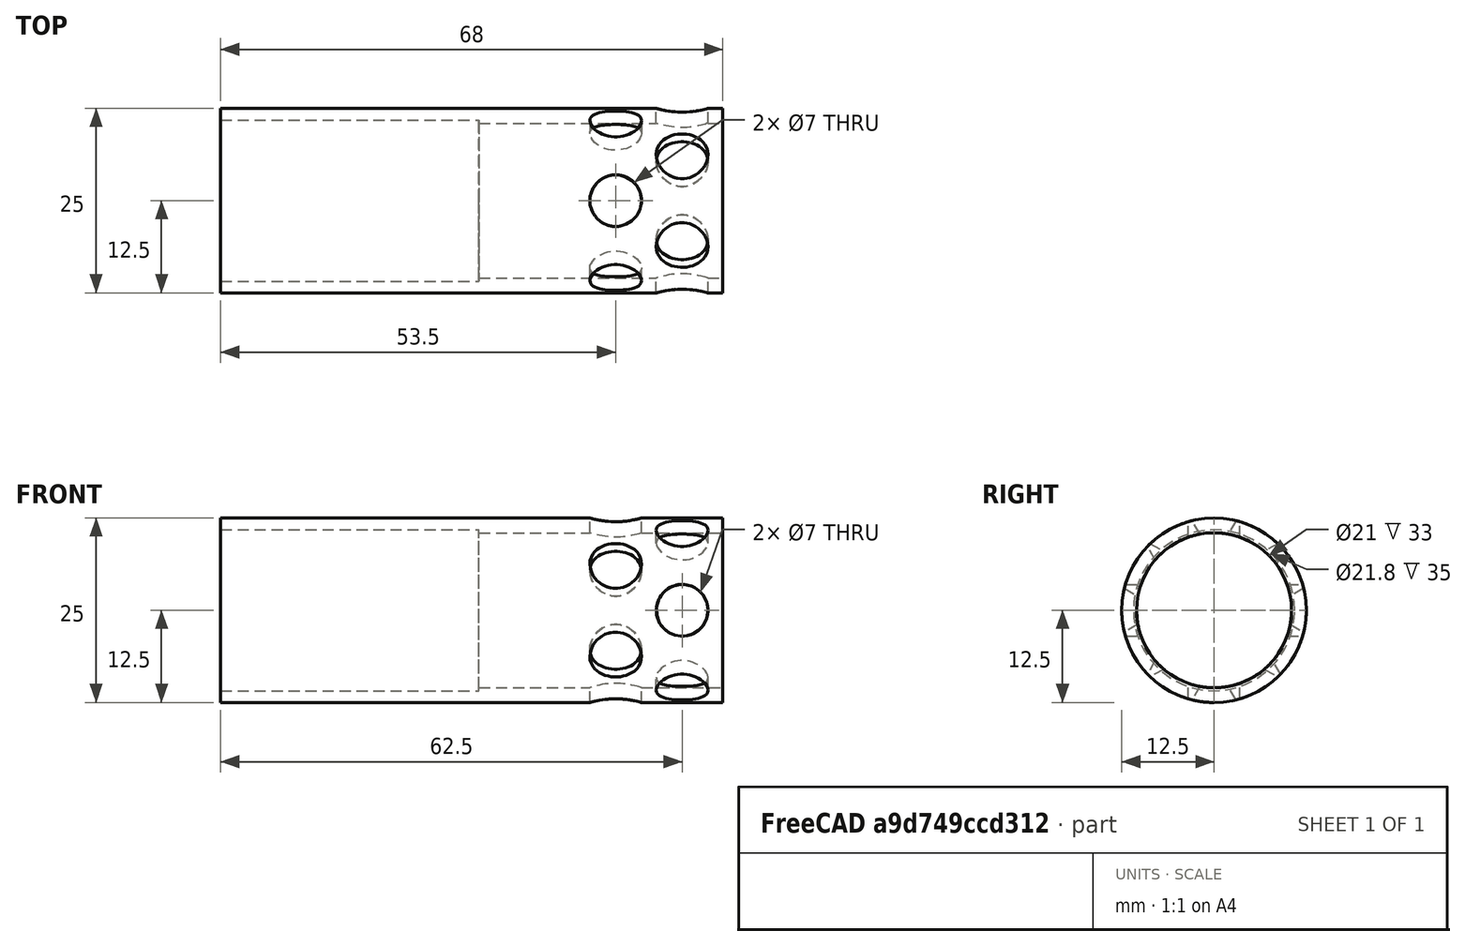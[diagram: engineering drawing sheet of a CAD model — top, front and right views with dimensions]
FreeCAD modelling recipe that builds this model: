
FCSTD DOCUMENT  (FreeCAD 0.17R13541 (Git))
Label: ERG-T-04-SC-01
License: All rights reserved
LicenseURL: http://en.wikipedia.org/wiki/All_rights_reserved
objects: Drawing::FeatureViewPython×12, Part::Cylinder×9, Part::MultiFuse×4, Part::Cut×2, Drawing::FeatureViewPart×2, Drawing::FeaturePage×1
note: 15 computed .brp shape members not serialized (recipe doc carries the construction recipe); baked Part::Feature solids carry a one-line shape summary decoded from their .brp

FEATURE [Part::Cylinder] Cylinder070  label="Cylinder075"
  Angle = 360
  AttacherType = Attacher::AttachEngine3D
  Height = 50
  Placement = pos=(214.2,-21.6506,12.5) rot=(-1,0,0;2.0944rad)
  Radius = 3.5
FEATURE [Part::Cylinder] Cylinder073  label="Cylinder082"
  Angle = 360
  AttacherType = Attacher::AttachEngine3D
  Height = 50
  Placement = pos=(214.2,-21.6506,12.5) rot=(-1,0,0;2.0944rad)
  Radius = 3.5
FEATURE [Part::Cylinder] Cylinder078  label="Cylinder087"
  Angle = 360
  AttacherType = Attacher::AttachEngine3D
  Height = 50
  Placement = pos=(214.2,21.6506,12.5) rot=(1,0,0;2.0944rad)
  Radius = 3.5
FEATURE [Part::Cylinder] Cylinder079  label="Cylinder088"
  Angle = 360
  AttacherType = Attacher::AttachEngine3D
  Height = 50
  Placement = pos=(214.2,21.6506,12.5) rot=(1,0,0;2.0944rad)
  Radius = 3.5
FEATURE [Part::Cylinder] Cylinder081  label="Cylinder090"
  Angle = 360
  AttacherType = Attacher::AttachEngine3D
  Height = 50
  Placement = pos=(214.2,0,-25) rot=(0,1,0;0rad)
  Radius = 3.5
FEATURE [Part::MultiFuse] Fusion016
  Placement = pos=(37.5,0,0) rot=(1,0,0;0rad)
  Shapes = -> [Cylinder081,Cylinder070,Cylinder078]
FEATURE [Part::Cylinder] Cylinder082  label="Cylinder078"
  Angle = 360
  AttacherType = Attacher::AttachEngine3D
  Height = 50
  Placement = pos=(214.2,0,-25) rot=(0,1,0;0rad)
  Radius = 3.5
FEATURE [Part::MultiFuse] Fusion018
  Placement = pos=(46.5,0,0) rot=(1,0,0;0.523599rad)
  Shapes = -> [Cylinder082,Cylinder073,Cylinder079]
FEATURE [Part::MultiFuse] Fusion  label="holesticks"
  Shapes = -> [Fusion016,Fusion018]
FEATURE [Part::Cylinder] Cylinder090  label="Cylinder098"
  Angle = 360
  AttacherType = Attacher::AttachEngine3D
  Height = 68
  Placement = pos=(198.2,0,0) rot=(0,1,0;1.5708rad)
  Radius = 12.5
FEATURE [Part::Cylinder] Cylinder071  label="Cylinder081"
  Angle = 360
  AttacherType = Attacher::AttachEngine3D
  Height = 33
  Placement = pos=(233.2,0,0) rot=(0,1,0;1.5708rad)
  Radius = 10.5
FEATURE [Part::Cylinder] Cylinder091  label="Cylinder099"
  Angle = 360
  AttacherType = Attacher::AttachEngine3D
  Height = 35
  Placement = pos=(198.2,0,0) rot=(0,1,0;1.5708rad)
  Radius = 10.9
FEATURE [Part::MultiFuse] Fusion019  label="cavity"
  Shapes = -> [Cylinder091,Cylinder071]
FEATURE [Part::Cut] Cut  label="body"
  Base = -> Cylinder090
  Tool = -> Fusion019
FEATURE [Part::Cut] Cut001  label="cap"
  Base = -> Cut
  Tool = -> Fusion
FEATURE [Drawing::FeatureViewPart] Ortho  label="Ortho_0_0"
  Direction = (1,0,0)
  HiddenWidth = 0.15
  LineWidth = 0.35
  Rotation = -90
  Scale = 2
  ShowHiddenLines = true
  ShowSmoothLines = false
  Source = -> Cut001
  Tolerance = 0.05
  ViewResult = <blob: 35669 chars omitted>
  Visible = true
  X = 65.3333
  Y = 81.5
FEATURE [Drawing::FeatureViewPart] Ortho001  label="Ortho_1_0"
  Direction = (0,1,0)
  HiddenWidth = 0.15
  LineWidth = 0.35
  Rotation = -90
  Scale = 2
  ShowHiddenLines = true
  ShowSmoothLines = false
  Source = -> Cut001
  Tolerance = 0.05
  ViewResult = <blob: 45142 chars omitted>
  Visible = true
  X = 653.067
  Y = 81.5
FEATURE [Drawing::FeatureViewPython] dim001  # drawing view (typed FeaturePython)
  Rotation = 0
  ViewResult = <g> \n  <line x1="120.667000" y1="56.500000" x2="120.667000" y2="35.635812" style="stroke:rgb(255,0,0);stroke-width:0.10" />\n<line x1="256.667000" y1="56.500000" x2="256.667000" y2="35.635812" style="stroke:rgb(255,0,0);stroke-width:0.10" />\n<line x1="120.667000" y1="36.635812" x2="256.667000" y2="36.635812" style="stroke:rgb(255,0,0);stroke-width:0.10" /> \n  <polygon points="256.667000,36.635812 254.667000,36.135812 254.167000,36.635812 254.667000,37.135812" style="fill:rgb(255,0,0);stroke:rgb(255,0,0);stroke-width:0" /><polygon points="120.667000,36.635812 122.667000,37.135812 123.167000,36.635812 122.667000,36.135812" style="fill:rgb(255,0,0);stroke:rgb(255,0,0);stroke-width:0" /> \n  <text x="188.667000" y="34.635812" font-family="inherit" font-size="3.6" fill="rgb(0,0,0)" text-anchor="middle" transform="rotate(0.000000 188.667000,34.635812)" >68</text> </g>
  Visible = true
  X = 0
  Y = 0
  arrowL1 = 2
  arrowL2 = 0.5
  arrowW = 1
  arrow_scheme = 0
  autoPlaceOffset = 2
  autoPlaceText = true
  click1_x = 255.659
  click1_y = 36.6358
  click2_x = 255.659
  click2_y = 36.6358
  comma_decimal_place = false
  dimension_line_overshoot = 1
  gap_datum_points = 0
  halfDimension_linear = false
  lineColor = rgb(255,0,0)
  strokeWidth = 0.1
  textFormat_linear = %(value)3.3f
  textRenderer_color = rgb(0,0,0)
  textRenderer_family = inherit
  textRenderer_size = 3.6
  unit_custom_scale = 1
  unit_scheme = 0
FEATURE [Drawing::FeatureViewPython] dim005  # drawing view (typed FeaturePython)
  Rotation = 0
  ViewResult = <g> \n  <line x1="256.667000" y1="106.500000" x2="279.698064" y2="106.500000" style="stroke:rgb(255,0,0);stroke-width:0.10" />\n<line x1="256.667000" y1="56.500000" x2="279.698064" y2="56.500000" style="stroke:rgb(255,0,0);stroke-width:0.10" />\n<line x1="278.698064" y1="106.500000" x2="278.698064" y2="56.500000" style="stroke:rgb(255,0,0);stroke-width:0.10" /> \n  <polygon points="278.698064,56.500000 278.198064,58.500000 278.698064,59.000000 279.198064,58.500000" style="fill:rgb(255,0,0);stroke:rgb(255,0,0);stroke-width:0" /><polygon points="278.698064,106.500000 279.198064,104.500000 278.698064,104.000000 278.198064,104.500000" style="fill:rgb(255,0,0);stroke:rgb(255,0,0);stroke-width:0" /> \n  <text x="276.698064" y="81.500000" font-family="inherit" font-size="3.6" fill="rgb(0,0,0)" text-anchor="middle" transform="rotate(-90.000000 276.698064,81.500000)" >25</text> </g>
  Visible = true
  X = 0
  Y = 0
  arrowL1 = 2
  arrowL2 = 0.5
  arrowW = 1
  arrow_scheme = 0
  autoPlaceOffset = 2
  autoPlaceText = true
  click1_x = 278.698
  click1_y = 57.3499
  click2_x = 278.698
  click2_y = 57.3499
  comma_decimal_place = false
  dimension_line_overshoot = 1
  gap_datum_points = 0
  halfDimension_linear = false
  lineColor = rgb(255,0,0)
  strokeWidth = 0.1
  textFormat_linear = %(value)3.3f
  textRenderer_color = rgb(0,0,0)
  textRenderer_family = inherit
  textRenderer_size = 3.6
  unit_custom_scale = 1
  unit_scheme = 0
FEATURE [Drawing::FeatureViewPython] dim006  # drawing view (typed FeaturePython)
  Rotation = 0
  ViewResult = <g> \n  <line x1="256.667000" y1="103.300000" x2="248.784893" y2="103.300000" style="stroke:rgb(255,0,0);stroke-width:0.10" />\n<line x1="256.667000" y1="59.700000" x2="248.784893" y2="59.700000" style="stroke:rgb(255,0,0);stroke-width:0.10" />\n<line x1="249.784893" y1="103.300000" x2="249.784893" y2="59.700000" style="stroke:rgb(255,0,0);stroke-width:0.10" /> \n  <polygon points="249.784893,59.700000 249.284893,61.700000 249.784893,62.200000 250.284893,61.700000" style="fill:rgb(255,0,0);stroke:rgb(255,0,0);stroke-width:0" /><polygon points="249.784893,103.300000 250.284893,101.300000 249.784893,100.800000 249.284893,101.300000" style="fill:rgb(255,0,0);stroke:rgb(255,0,0);stroke-width:0" /> \n  <text x="247.784893" y="81.500000" font-family="inherit" font-size="3.6" fill="rgb(0,0,0)" text-anchor="middle" transform="rotate(-90.000000 247.784893,81.500000)" >21.8</text> </g>
  Visible = true
  X = 0
  Y = 0
  arrowL1 = 2
  arrowL2 = 0.5
  arrowW = 1
  arrow_scheme = 0
  autoPlaceOffset = 2
  autoPlaceText = true
  click1_x = 249.785
  click1_y = 59.7094
  click2_x = 249.785
  click2_y = 59.7094
  comma_decimal_place = false
  dimension_line_overshoot = 1
  gap_datum_points = 0
  halfDimension_linear = false
  lineColor = rgb(255,0,0)
  strokeWidth = 0.1
  textFormat_linear = %(value)3.3f
  textRenderer_color = rgb(0,0,0)
  textRenderer_family = inherit
  textRenderer_size = 3.6
  unit_custom_scale = 1
  unit_scheme = 0
FEATURE [Drawing::FeatureViewPython] dim007  # drawing view (typed FeaturePython)
  Rotation = 0
  ViewResult = <g> \n  <line x1="120.667000" y1="106.500000" x2="120.667000" y2="116.625500" style="stroke:rgb(255,0,0);stroke-width:0.10" />\n<line x1="131.667000" y1="105.784600" x2="131.667000" y2="116.625500" style="stroke:rgb(255,0,0);stroke-width:0.10" />\n<line x1="120.667000" y1="115.625500" x2="131.667000" y2="115.625500" style="stroke:rgb(255,0,0);stroke-width:0.10" /> \n  <polygon points="131.667000,115.625500 129.667000,115.125500 129.167000,115.625500 129.667000,116.125500" style="fill:rgb(255,0,0);stroke:rgb(255,0,0);stroke-width:0" /><polygon points="120.667000,115.625500 122.667000,116.125500 123.167000,115.625500 122.667000,115.125500" style="fill:rgb(255,0,0);stroke:rgb(255,0,0);stroke-width:0" /> \n  <text x="126.167000" y="113.625500" font-family="inherit" font-size="3.6" fill="rgb(0,0,0)" text-anchor="middle" transform="rotate(0.000000 126.167000,113.625500)" >5.5</text> </g>
  Visible = true
  X = 0
  Y = 0
  arrowL1 = 2
  arrowL2 = 0.5
  arrowW = 1
  arrow_scheme = 0
  autoPlaceOffset = 2
  autoPlaceText = true
  click1_x = 131.265
  click1_y = 115.625
  click2_x = 131.265
  click2_y = 115.625
  comma_decimal_place = false
  dimension_line_overshoot = 1
  gap_datum_points = 0
  halfDimension_linear = false
  lineColor = rgb(255,0,0)
  strokeWidth = 0.1
  textFormat_linear = %(value)3.3f
  textRenderer_color = rgb(0,0,0)
  textRenderer_family = inherit
  textRenderer_size = 3.6
  unit_custom_scale = 1
  unit_scheme = 0
FEATURE [Drawing::FeatureViewPython] dim008  # drawing view (typed FeaturePython)
  Rotation = 0
  ViewResult = <g> \n  <line x1="120.667000" y1="106.500000" x2="120.667000" y2="128.175501" style="stroke:rgb(255,0,0);stroke-width:0.10" />\n<line x1="149.667000" y1="105.500000" x2="149.667000" y2="128.175501" style="stroke:rgb(255,0,0);stroke-width:0.10" />\n<line x1="120.667000" y1="127.175501" x2="149.667000" y2="127.175501" style="stroke:rgb(255,0,0);stroke-width:0.10" /> \n  <polygon points="149.667000,127.175501 147.667000,126.675501 147.167000,127.175501 147.667000,127.675501" style="fill:rgb(255,0,0);stroke:rgb(255,0,0);stroke-width:0" /><polygon points="120.667000,127.175501 122.667000,127.675501 123.167000,127.175501 122.667000,126.675501" style="fill:rgb(255,0,0);stroke:rgb(255,0,0);stroke-width:0" /> \n  <text x="135.167000" y="125.175501" font-family="inherit" font-size="3.6" fill="rgb(0,0,0)" text-anchor="middle" transform="rotate(0.000000 135.167000,125.175501)" >14.5</text> </g>
  Visible = true
  X = 0
  Y = 0
  arrowL1 = 2
  arrowL2 = 0.5
  arrowW = 1
  arrow_scheme = 0
  autoPlaceOffset = 2
  autoPlaceText = true
  click1_x = 142.693
  click1_y = 127.176
  click2_x = 142.693
  click2_y = 127.176
  comma_decimal_place = false
  dimension_line_overshoot = 1
  gap_datum_points = 0
  halfDimension_linear = false
  lineColor = rgb(255,0,0)
  strokeWidth = 0.1
  textFormat_linear = %(value)3.3f
  textRenderer_color = rgb(0,0,0)
  textRenderer_family = inherit
  textRenderer_size = 3.6
  unit_custom_scale = 1
  unit_scheme = 0
FEATURE [Drawing::FeatureViewPython] dia003  # drawing view (typed FeaturePython)
  Rotation = 0
  ViewResult = <g>  <circle cx ="131.660789" cy ="81.491584" r="0.250000" stroke="none" fill="rgb(255,0,0)" /> \n<line x1="117.784889" y1="96.081933" x2="136.477774" y2="76.426580" style="stroke:rgb(255,0,0);stroke-width:0.10" />\n<polygon points="126.843804,86.556588 128.584403,85.451908 128.566661,84.745024 127.859777,84.762765" style="fill:rgb(255,0,0);stroke:rgb(255,0,0);stroke-width:0" />\n<polygon points="136.477774,76.426580 134.737176,77.531260 134.754917,78.238144 135.461801,78.220403" style="fill:rgb(255,0,0);stroke:rgb(255,0,0);stroke-width:0" />\n<line x1="117.784889" y1="96.081933" x2="108.296662" y2="96.081933" style="stroke:rgb(255,0,0);stroke-width:0.10" />\n<text x="113.040776" y="94.081933" font-family="inherit" font-size="3.6" fill="rgb(0,0,0)" text-anchor="middle" transform="rotate(0.000000 113.040776,94.081933)" >Ø6.99</text> </g>
  Visible = true
  X = 0
  Y = 0
  arrowL1 = 2
  arrowL2 = 0.5
  arrowW = 1
  arrow_scheme = 0
  autoPlaceOffset = 2
  autoPlaceText = true
  centerPointDia = 0.5
  click1_x = 117.785
  click1_y = 96.0819
  click2_x = 108.297
  click2_y = 96.2455
  click3_x = 108.297
  click3_y = 96.2455
  comma_decimal_place = false
  lineColor = rgb(255,0,0)
  strokeWidth = 0.1
  textFormat_circular = Ø%(value)3.3f
  textRenderer_color = rgb(0,0,0)
  textRenderer_family = inherit
  textRenderer_size = 3.6
  unit_custom_scale = 1
  unit_scheme = 0
FEATURE [Drawing::FeatureViewPython] dim002  # drawing view (typed FeaturePython)
  Rotation = 0
  ViewResult = <g> \n  <line x1="120.667000" y1="56.500000" x2="120.667000" y2="46.120743" style="stroke:rgb(255,0,0);stroke-width:0.10" />\n<line x1="186.667000" y1="59.700000" x2="186.667000" y2="46.120743" style="stroke:rgb(255,0,0);stroke-width:0.10" />\n<line x1="120.667000" y1="47.120743" x2="186.667000" y2="47.120743" style="stroke:rgb(255,0,0);stroke-width:0.10" /> \n  <polygon points="186.667000,47.120743 184.667000,46.620743 184.167000,47.120743 184.667000,47.620743" style="fill:rgb(255,0,0);stroke:rgb(255,0,0);stroke-width:0" /><polygon points="120.667000,47.120743 122.667000,47.620743 123.167000,47.120743 122.667000,46.620743" style="fill:rgb(255,0,0);stroke:rgb(255,0,0);stroke-width:0" /> \n  <text x="153.667000" y="45.120743" font-family="inherit" font-size="3.6" fill="rgb(0,0,0)" text-anchor="middle" transform="rotate(0.000000 153.667000,45.120743)" >33</text> </g>
  Visible = true
  X = 0
  Y = 0
  arrowL1 = 2
  arrowL2 = 0.5
  arrowW = 1
  arrow_scheme = 0
  autoPlaceOffset = 2
  autoPlaceText = true
  click1_x = 185.329
  click1_y = 47.1207
  click2_x = 185.329
  click2_y = 47.1207
  comma_decimal_place = false
  dimension_line_overshoot = 1
  gap_datum_points = 0
  halfDimension_linear = false
  lineColor = rgb(255,0,0)
  strokeWidth = 0.1
  textFormat_linear = %(value)3.3f
  textRenderer_color = rgb(0,0,0)
  textRenderer_family = inherit
  textRenderer_size = 3.6
  unit_custom_scale = 1
  unit_scheme = 0
FEATURE [Drawing::FeatureViewPython] dim003  # drawing view (typed FeaturePython)
  Rotation = 0
  ViewResult = <g> \n  <line x1="186.667000" y1="59.700000" x2="186.667000" y2="46.151662" style="stroke:rgb(255,0,0);stroke-width:0.10" />\n<line x1="256.667000" y1="56.500000" x2="256.667000" y2="46.151662" style="stroke:rgb(255,0,0);stroke-width:0.10" />\n<line x1="186.667000" y1="47.151662" x2="256.667000" y2="47.151662" style="stroke:rgb(255,0,0);stroke-width:0.10" /> \n  <polygon points="256.667000,47.151662 254.667000,46.651662 254.167000,47.151662 254.667000,47.651662" style="fill:rgb(255,0,0);stroke:rgb(255,0,0);stroke-width:0" /><polygon points="186.667000,47.151662 188.667000,47.651662 189.167000,47.151662 188.667000,46.651662" style="fill:rgb(255,0,0);stroke:rgb(255,0,0);stroke-width:0" /> \n  <text x="221.667000" y="45.151662" font-family="inherit" font-size="3.6" fill="rgb(0,0,0)" text-anchor="middle" transform="rotate(0.000000 221.667000,45.151662)" >35</text> </g>
  Visible = true
  X = 0
  Y = 0
  arrowL1 = 2
  arrowL2 = 0.5
  arrowW = 1
  arrow_scheme = 0
  autoPlaceOffset = 2
  autoPlaceText = true
  click1_x = 193.476
  click1_y = 47.1517
  click2_x = 193.476
  click2_y = 47.1517
  comma_decimal_place = false
  dimension_line_overshoot = 1
  gap_datum_points = 0
  halfDimension_linear = false
  lineColor = rgb(255,0,0)
  strokeWidth = 0.1
  textFormat_linear = %(value)3.3f
  textRenderer_color = rgb(0,0,0)
  textRenderer_family = inherit
  textRenderer_size = 3.6
  unit_custom_scale = 1
  unit_scheme = 0
FEATURE [Drawing::FeatureViewPython] dim004  # drawing view (typed FeaturePython)
  Rotation = 0
  ViewResult = <g> \n  <line x1="186.667000" y1="60.500000" x2="177.326040" y2="60.500000" style="stroke:rgb(255,0,0);stroke-width:0.10" />\n<line x1="186.667000" y1="102.500000" x2="177.326040" y2="102.500000" style="stroke:rgb(255,0,0);stroke-width:0.10" />\n<line x1="178.326040" y1="60.500000" x2="178.326040" y2="102.500000" style="stroke:rgb(255,0,0);stroke-width:0.10" /> \n  <polygon points="178.326040,102.500000 178.826040,100.500000 178.326040,100.000000 177.826040,100.500000" style="fill:rgb(255,0,0);stroke:rgb(255,0,0);stroke-width:0" /><polygon points="178.326040,60.500000 177.826040,62.500000 178.326040,63.000000 178.826040,62.500000" style="fill:rgb(255,0,0);stroke:rgb(255,0,0);stroke-width:0" /> \n  <text x="176.326040" y="81.500000" font-family="inherit" font-size="3.6" fill="rgb(0,0,0)" text-anchor="middle" transform="rotate(-90.000000 176.326040,81.500000)" >21</text> </g>
  Visible = true
  X = 0
  Y = 0
  arrowL1 = 2
  arrowL2 = 0.5
  arrowW = 1
  arrow_scheme = 0
  autoPlaceOffset = 2
  autoPlaceText = true
  click1_x = 178.326
  click1_y = 102.033
  click2_x = 178.326
  click2_y = 102.033
  comma_decimal_place = false
  dimension_line_overshoot = 1
  gap_datum_points = 0
  halfDimension_linear = false
  lineColor = rgb(255,0,0)
  strokeWidth = 0.1
  textFormat_linear = %(value)3.3f
  textRenderer_color = rgb(0,0,0)
  textRenderer_family = inherit
  textRenderer_size = 3.6
  unit_custom_scale = 1
  unit_scheme = 0
FEATURE [Drawing::FeatureViewPython] dia001  # drawing view (typed FeaturePython)
  Rotation = 0
  ViewResult = <g>  <circle cx ="65.342548" cy ="81.518015" r="0.250000" stroke="none" fill="rgb(255,0,0)" /> \n<line x1="86.877068" y1="120.611789" x2="55.200587" y2="63.106296" style="stroke:rgb(255,0,0);stroke-width:0.10" />\n<polygon points="75.484510,99.929735 74.957491,97.936684 74.278296,97.739975 74.081587,98.419170" style="fill:rgb(255,0,0);stroke:rgb(255,0,0);stroke-width:0" />\n<polygon points="55.200587,63.106296 55.727606,65.099346 56.406801,65.296056 56.603510,64.616861" style="fill:rgb(255,0,0);stroke:rgb(255,0,0);stroke-width:0" />\n<line x1="86.877068" y1="120.611789" x2="99.883225" y2="120.611789" style="stroke:rgb(255,0,0);stroke-width:0.10" />\n<text x="93.380146" y="118.611789" font-family="inherit" font-size="3.6" fill="rgb(0,0,0)" text-anchor="middle" transform="rotate(0.000000 93.380146,118.611789)" >Ø21.02</text> </g>
  Visible = true
  X = 0
  Y = 0
  arrowL1 = 2
  arrowL2 = 0.5
  arrowW = 1
  arrow_scheme = 0
  autoPlaceOffset = 2
  autoPlaceText = true
  centerPointDia = 0.5
  click1_x = 86.8771
  click1_y = 120.612
  click2_x = 99.8832
  click2_y = 121.018
  click3_x = 99.8832
  click3_y = 121.018
  comma_decimal_place = false
  lineColor = rgb(255,0,0)
  strokeWidth = 0.1
  textFormat_circular = Ø%(value)3.3f
  textRenderer_color = rgb(0,0,0)
  textRenderer_family = inherit
  textRenderer_size = 3.6
  unit_custom_scale = 1
  unit_scheme = 0
FEATURE [Drawing::FeatureViewPython] dia002  # drawing view (typed FeaturePython)
  Rotation = 0
  ViewResult = <g>  <circle cx ="65.333300" cy ="81.500000" r="0.250000" stroke="none" fill="rgb(255,0,0)" /> \n<line x1="41.253906" y1="120.103736" x2="76.870754" y2="63.003321" style="stroke:rgb(255,0,0);stroke-width:0.10" />\n<polygon points="53.795846,99.996679 55.278564,98.564357 55.118948,97.875501 54.430092,98.035116" style="fill:rgb(255,0,0);stroke:rgb(255,0,0);stroke-width:0" />\n<polygon points="76.870754,63.003321 75.388036,64.435643 75.547652,65.124499 76.236508,64.964884" style="fill:rgb(255,0,0);stroke:rgb(255,0,0);stroke-width:0" />\n<line x1="41.253906" y1="120.103736" x2="30.584792" y2="120.103736" style="stroke:rgb(255,0,0);stroke-width:0.10" />\n<text x="35.919349" y="118.103736" font-family="inherit" font-size="3.6" fill="rgb(0,0,0)" text-anchor="middle" transform="rotate(0.000000 35.919349,118.103736)" >Ø21.8</text> </g>
  Visible = true
  X = 0
  Y = 0
  arrowL1 = 2
  arrowL2 = 0.5
  arrowW = 1
  arrow_scheme = 0
  autoPlaceOffset = 2
  autoPlaceText = true
  centerPointDia = 0.5
  click1_x = 41.2539
  click1_y = 120.104
  click2_x = 30.5848
  click2_y = 119.189
  click3_x = 30.5848
  click3_y = 119.189
  comma_decimal_place = false
  lineColor = rgb(255,0,0)
  strokeWidth = 0.1
  textFormat_circular = Ø%(value)3.3f
  textRenderer_color = rgb(0,0,0)
  textRenderer_family = inherit
  textRenderer_size = 3.6
  unit_custom_scale = 1
  unit_scheme = 0
FEATURE [Drawing::FeatureViewPython] dia004  # drawing view (typed FeaturePython)
  Rotation = 0
  ViewResult = <g>  <circle cx ="65.333300" cy ="81.500000" r="0.250000" stroke="none" fill="rgb(255,0,0)" /> \n<line x1="100.086446" y1="52.837515" x2="46.046554" y2="97.406648" style="stroke:rgb(255,0,0);stroke-width:0.10" />\n<polygon points="84.620046,65.593352 82.758973,66.480149 82.691371,67.184017 83.395239,67.251619" style="fill:rgb(255,0,0);stroke:rgb(255,0,0);stroke-width:0" />\n<polygon points="46.046554,97.406648 47.907627,96.519851 47.975229,95.815983 47.271361,95.748381" style="fill:rgb(255,0,0);stroke:rgb(255,0,0);stroke-width:0" />\n<line x1="100.086446" y1="52.837515" x2="110.755560" y2="52.837515" style="stroke:rgb(255,0,0);stroke-width:0.10" />\n<text x="105.421003" y="50.837515" font-family="inherit" font-size="3.6" fill="rgb(0,0,0)" text-anchor="middle" transform="rotate(0.000000 105.421003,50.837515)" >Ø25</text> </g>
  Visible = true
  X = 0
  Y = 0
  arrowL1 = 2
  arrowL2 = 0.5
  arrowW = 1
  arrow_scheme = 0
  autoPlaceOffset = 2
  autoPlaceText = true
  centerPointDia = 0.5
  click1_x = 100.086
  click1_y = 52.8375
  click2_x = 110.756
  click2_y = 52.8375
  click3_x = 110.756
  click3_y = 52.8375
  comma_decimal_place = false
  lineColor = rgb(255,0,0)
  strokeWidth = 0.1
  textFormat_circular = Ø%(value)3.3f
  textRenderer_color = rgb(0,0,0)
  textRenderer_family = inherit
  textRenderer_size = 3.6
  unit_custom_scale = 1
  unit_scheme = 0
FEATURE [Drawing::FeaturePage] Page
  EditableTexts = Dr. Zoidberg | 24.10.2019	 | x2 | ERG-T-04 | Sensor Cap	 | 1 | 1
  Group = -> [Ortho,Ortho001,dim001,dim005,dim006,dim007,dim008,dia003,dim002,dim003,dim004,dia001,dia002,dia004]
  Template = <path>//share/freecad/Mod/Drawing/Templates/A4_Landscape.svg
note: 1 file-system path scrubbed to <path> (originals preserved in the JSON sidecar)
